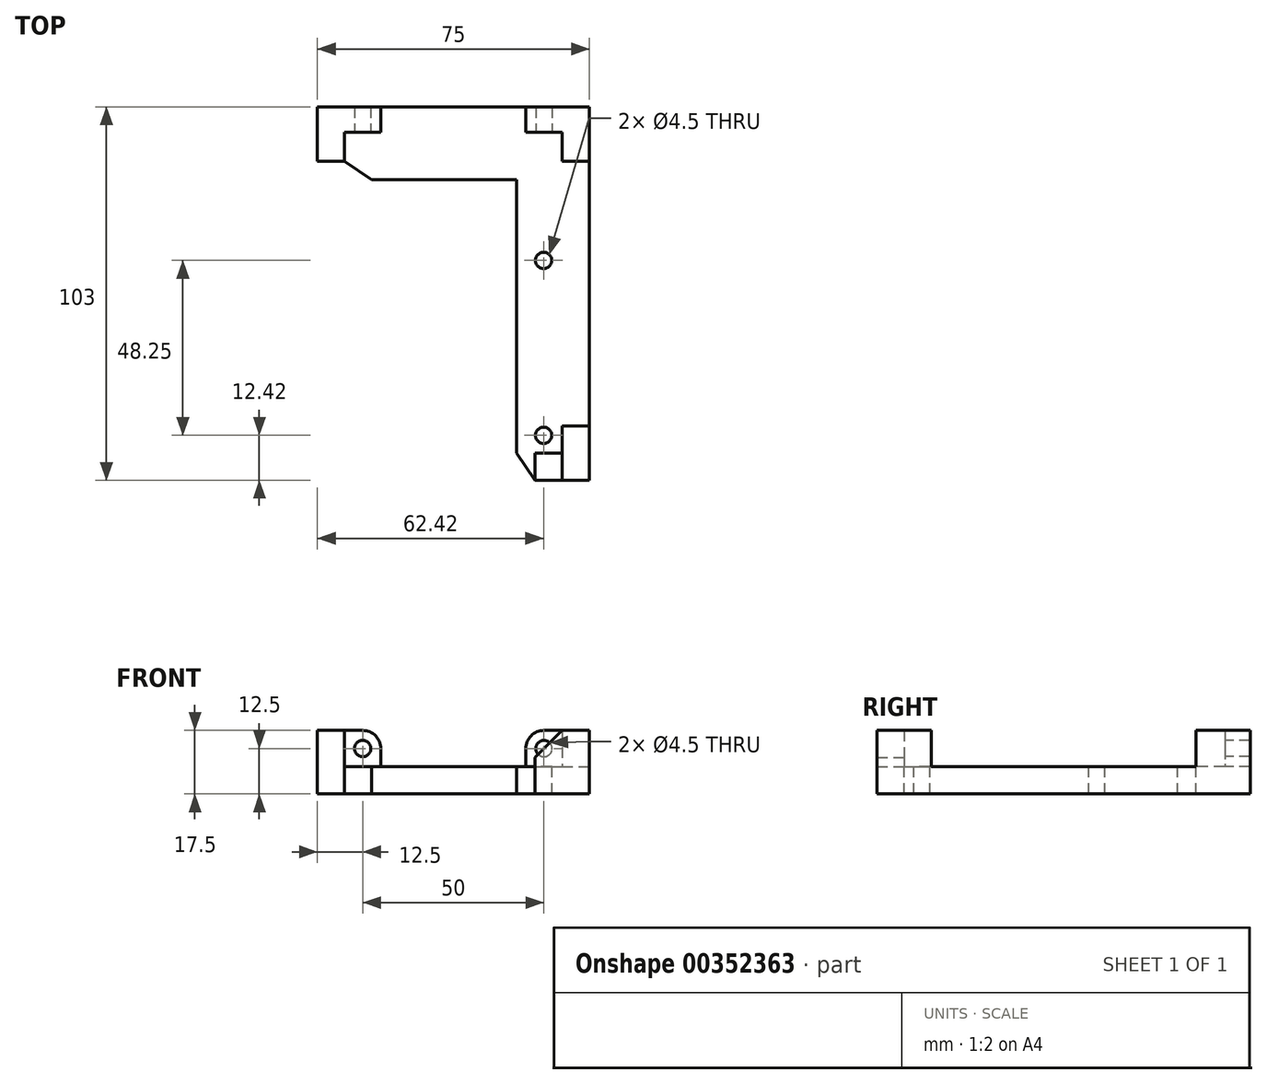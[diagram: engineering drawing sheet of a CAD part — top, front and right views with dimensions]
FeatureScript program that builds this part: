
annotation { "Feature Type Name" : "Feature", "Feature Type Description" : "" }
export const myFeature = defineFeature(function(context is Context, id is Id, definition is map)
    precondition{}
    {
        {
            var Q0;
            Q0=qCreatedBy(makeId("Top.planeOp"),FACE);
            var sketch = newSketch(context, id + "F0", { "sketchPlane" : qUnion([Q0])});
            skLineSegment(sketch, "E0.bottom", {"start": v(-37.5, 51.5) * mm, "end": v(37.5, 51.5) * mm});
            skLineSegment(sketch, "E0.right", {"start": v(37.5, 51.5) * mm, "end": v(37.5, -51.5) * mm});
            skPoint(sketch, "E0.middle", {"position": v(0, 0) * mm});
            skLineSegment(sketch, "E1", {"start": v(22.5, -51.5) * mm, "end": v(22.5, -44) * mm});
            skLineSegment(sketch, "E2", {"start": v(22.5, -44) * mm, "end": v(30, -44) * mm});
            skLineSegment(sketch, "E3", {"start": v(30, -44) * mm, "end": v(30, -36.5) * mm});
            skLineSegment(sketch, "E4", {"start": v(30, -36.5) * mm, "end": v(37.5, -36.5) * mm});
            skLineSegment(sketch, "E5", {"start": v(37.5, -36.5) * mm, "end": v(37.5, -51.5) * mm});
            skLineSegment(sketch, "E6", {"start": v(-37.5, 36.5) * mm, "end": v(-30, 36.5) * mm});
            skLineSegment(sketch, "E7", {"start": v(-30, 36.5) * mm, "end": v(-30, 44.5) * mm});
            skLineSegment(sketch, "E8", {"start": v(-30, 44.5) * mm, "end": v(-20, 44.5) * mm});
            skLineSegment(sketch, "E9", {"start": v(-20, 44.5) * mm, "end": v(-20, 51.5) * mm});
            skLineSegment(sketch, "E10", {"start": v(-20, 51.5) * mm, "end": v(-37.5, 51.5) * mm});
            skLineSegment(sketch, "E11", {"start": v(20, 51.5) * mm, "end": v(20, 44.5) * mm});
            skLineSegment(sketch, "E12", {"start": v(20, 44.5) * mm, "end": v(30, 44.5) * mm});
            skLineSegment(sketch, "E13", {"start": v(30, 44.5) * mm, "end": v(30, 36.5) * mm});
            skLineSegment(sketch, "E14", {"start": v(30, 36.5) * mm, "end": v(37.5, 36.5) * mm});
            skLineSegment(sketch, "E15", {"start": v(37.5, 36.5) * mm, "end": v(37.5, 51.5) * mm});
            skLineSegment(sketch, "E16", {"start": v(-20, 44.5) * mm, "end": v(20, 44.5) * mm});
            skLineSegment(sketch, "E17", {"start": v(-37.5, 36.5) * mm, "end": v(-37.5, 51.5) * mm});
            skLineSegment(sketch, "E18", {"start": v(37.5, -51.5) * mm, "end": v(22.5, -51.5) * mm});
            skLineSegment(sketch, "E19", {"start": v(17.5, -44.01) * mm, "end": v(17.5, 44.5) * mm});
            skLineSegment(sketch, "E20", {"start": v(22.5, -51.5) * mm, "end": v(17.5, -44.01) * mm});
            skCircle(sketch, "E21", {"center": v(24.92, 9.17) * mm, "radius": 2.25 * mm});
            skCircle(sketch, "E22", {"center": v(24.92, -39.08) * mm, "radius": 2.25 * mm});
            skLineSegment(sketch, "E23", {"start": v(30, -36.5) * mm, "end": v(30, 36.5) * mm});
            skLineSegment(sketch, "E24", {"start": v(-22.5, 31.5) * mm, "end": v(17.5, 31.5) * mm});
            skLineSegment(sketch, "E25", {"start": v(-22.5, 31.5) * mm, "end": v(-30, 36.5) * mm});
            skSolve(sketch);
        }
        {
            var Q0;
            Q0=makeQuery(id+"F0.imprint","IMPRINT",FACE,{"disambiguationData":[TD([[makeQuery(id+"F0.imprint","IMPRINT",EDGE,{"derivedFrom":sQuery(id+"F0.wireOp",EDGE,"E0.right")}),-1.0]])]});
            var Q1;
            Q1=makeQuery(id+"F0.imprint","IMPRINT",FACE,{"disambiguationData":[TD([[makeQuery(id+"F0.imprint","IMPRINT",EDGE,{"derivedFrom":sQuery(id+"F0.wireOp",EDGE,"E1")}),-1.0]])]});
            var Q2;
            Q2=makeQuery(id+"F0.imprint","IMPRINT",FACE,{"disambiguationData":[TD([[makeQuery(id+"F0.imprint","IMPRINT",EDGE,{"derivedFrom":sQuery(id+"F0.wireOp",EDGE,"E1")}),1.0]])]});
            var Q3;
            {var subQ0=sQuery(id+"F0.wireOp",EDGE,"E11");Q3=makeQuery(id+"F0.imprint","IMPRINT",FACE,{"disambiguationData":[TD([[makeQuery(id+"F0.imprint","IMPRINT",EDGE,{"derivedFrom":subQ0}),1.0]])]});}
            var Q4;
            {var subQ1=sQuery(id+"F0.wireOp",EDGE,"E9");Q4=makeQuery(id+"F0.imprint","IMPRINT",FACE,{"disambiguationData":[TD([[makeQuery(id+"F0.imprint","IMPRINT",EDGE,{"derivedFrom":subQ1}),-1.0]])]});}
            var Q5;
            Q5=makeQuery(id+"F0.imprint","IMPRINT",FACE,{"disambiguationData":[TD([[makeQuery(id+"F0.imprint","IMPRINT",EDGE,{"derivedFrom":sQuery(id+"F0.wireOp",EDGE,"E6")}),1.0]])]});
            var Q6;
            Q6=makeQuery(id+"F0.imprint","IMPRINT",FACE,{"disambiguationData":[TD([[makeQuery(id+"F0.imprint","IMPRINT",EDGE,{"derivedFrom":sQuery(id+"F0.wireOp",EDGE,"E7")}),-1.0]])]});
            extrude(context, id + "F1", {"entities" : qUnion([Q0, Q1, Q2, Q3, Q4, Q5, Q6]), "oppositeDirection" : true, "depth" : 7.5 * mm});
        }
        {
            var Q0;
            {var subQ0=sQuery(id+"F0.wireOp",EDGE,"E11");Q0=makeQuery(id+"F0.imprint","IMPRINT",FACE,{"disambiguationData":[TD([[makeQuery(id+"F0.imprint","IMPRINT",EDGE,{"derivedFrom":subQ0}),1.0]])]});}
            var Q1;
            Q1=makeQuery(id+"F0.imprint","IMPRINT",FACE,{"disambiguationData":[TD([[makeQuery(id+"F0.imprint","IMPRINT",EDGE,{"derivedFrom":sQuery(id+"F0.wireOp",EDGE,"E1")}),-1.0]])]});
            var Q2;
            Q2=makeQuery(id+"F0.imprint","IMPRINT",FACE,{"disambiguationData":[TD([[makeQuery(id+"F0.imprint","IMPRINT",EDGE,{"derivedFrom":sQuery(id+"F0.wireOp",EDGE,"E6")}),1.0]])]});
            extrude(context, id + "F2", {"entities" : qUnion([Q0, Q1, Q2]), "operationType" : NewBodyOperationType.ADD, "depth" : 10 * mm});
        }
        {
            var Q0;
            Q0=qCreatedBy(makeId("Front.planeOp"),FACE);
            var sketch = newSketch(context, id + "F3", { "sketchPlane" : qUnion([Q0])});
            skCircle(sketch, "E26", {"center": v(25, 5) * mm, "radius": 2.25 * mm});
            skCircle(sketch, "E27", {"center": v(-25, 5) * mm, "radius": 2.25 * mm});
            skSolve(sketch);
        }
        {
            var Q0;
            Q0=makeQuery(id+"F3.imprint","IMPRINT",FACE,{"disambiguationData":[TD([[makeQuery(id+"F3.imprint","IMPRINT",EDGE,{"derivedFrom":sQuery(id+"F3.wireOp",EDGE,"E26")}),1.0]])]});
            var Q1;
            Q1=makeQuery(id+"F3.imprint","IMPRINT",FACE,{"disambiguationData":[TD([[makeQuery(id+"F3.imprint","IMPRINT",EDGE,{"derivedFrom":sQuery(id+"F3.wireOp",EDGE,"E27")}),1.0]])]});
            extrude(context, id + "F4", {"entities" : qUnion([Q0, Q1]), "operationType" : NewBodyOperationType.REMOVE, "oppositeDirection" : true, "depth" : 75 * mm});
        }
        {
            var Q0;
            Q0=makeQuery(id+"F2.opExtrude","CAP_EDGE",EDGE,{"disambiguationData":[OSD([sQuery(id+"F0.wireOp",EDGE,"E1")])],"isStart":false});
            chamfer(context, id + "F5", {"entities" : qUnion([Q0]), "width" : 7.5 * mm, "tangentPropagation" : true});
        }
        {
            var Q0;
            Q0=makeQuery(id+"F2.opExtrude","CAP_EDGE",EDGE,{"disambiguationData":[OSD([sQuery(id+"F0.wireOp",EDGE,"E9")])],"isStart":false});
            var Q1;
            Q1=makeQuery(id+"F2.opExtrude","CAP_EDGE",EDGE,{"disambiguationData":[OSD([sQuery(id+"F0.wireOp",EDGE,"E11")])],"isStart":false});
            fillet(context, id + "F6", {"entities" : qUnion([Q0, Q1]), "radius" : 5 * mm, "tangentPropagation" : true, "allowEdgeOverflow" : false});
        }
    });
